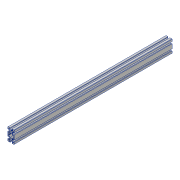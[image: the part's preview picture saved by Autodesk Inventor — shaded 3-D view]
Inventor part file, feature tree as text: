
AUTODESK INVENTOR PART (.ipt)
format: ipt  version: 2018 (Build 220112000, 112)  size: 243,712 bytes
history: native  units: mm
features: extrude x1, sketch x1
ambient origin geometry x8: Origin, YZ Plane, XZ Plane, XY Plane, X Axis, Y Axis, Z Axis, Center Point
bodies: Solid1 (feature_tree)
feature tree (2):
  extrude  "Extrusion1"  [1 undecoded]
  sketch  "Sketch1"  dims[d0=500.0mm d1=0.0mm]
note: 1 required parameter value undecoded (feature->parameter linkage not recoverable at this tier; creation-order binding heuristic only, values carry confidence <= 0.55)
